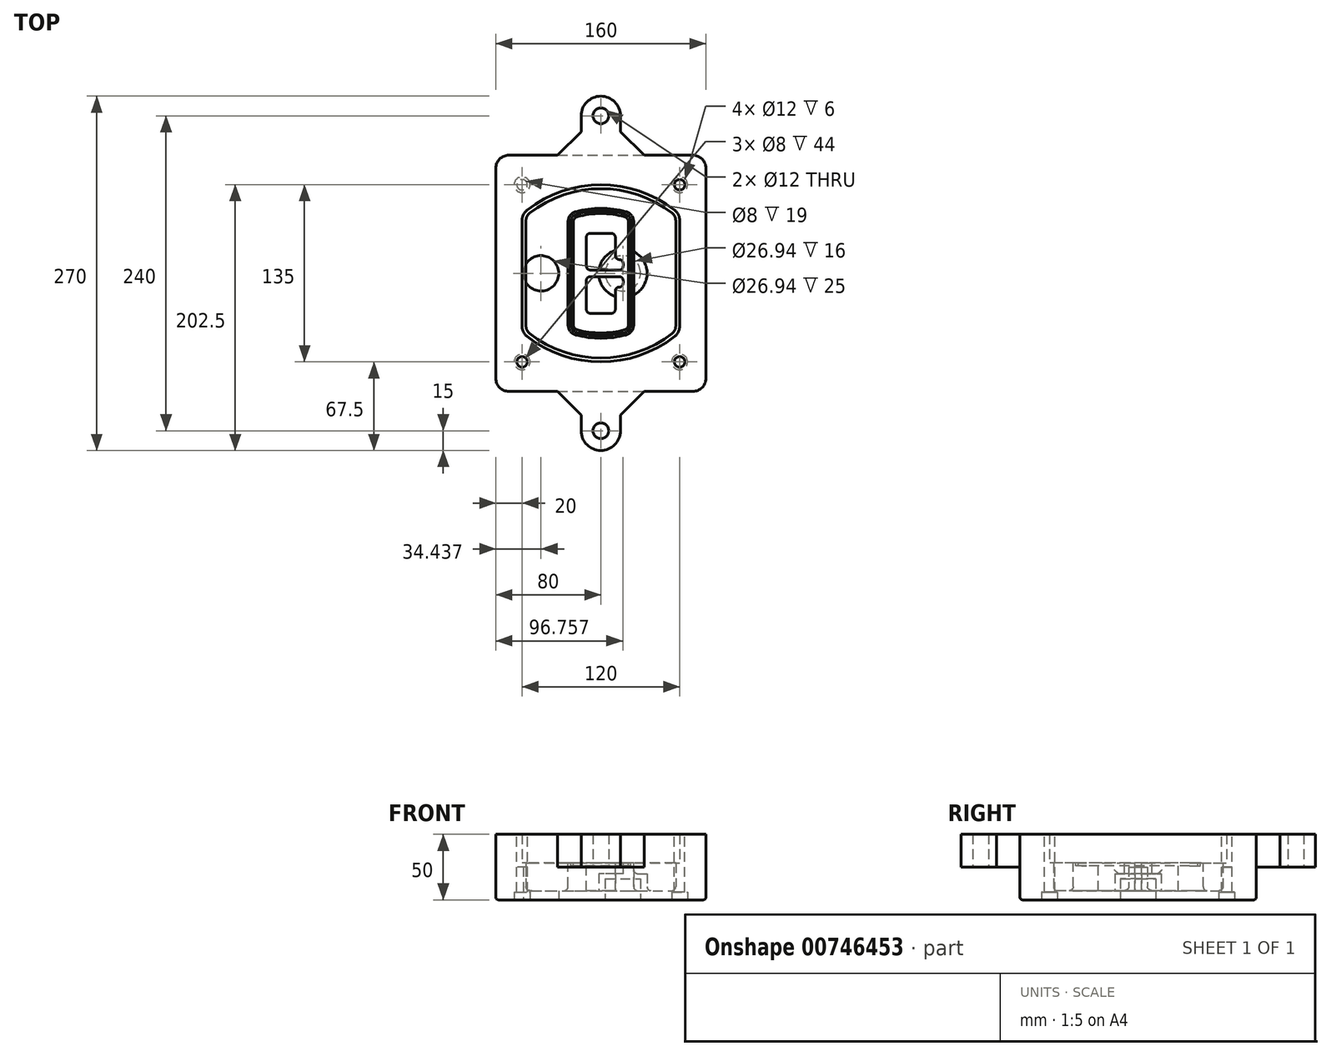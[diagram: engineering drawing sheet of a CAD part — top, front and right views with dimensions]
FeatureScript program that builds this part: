
annotation { "Feature Type Name" : "Feature", "Feature Type Description" : "" }
export const myFeature = defineFeature(function(context is Context, id is Id, definition is map)
    precondition{}
    {
        {
            var Q0;
            Q0=qCreatedBy(makeId("Top.planeOp"),FACE);
            var sketch = newSketch(context, id + "F0", { "sketchPlane" : qUnion([Q0])});
            skPoint(sketch, "E0.rect.middle", {"position": v(0, 0) * mm});
            skLineSegment(sketch, "E1.bottom", {"start": v(-70, -90) * mm, "end": v(70, -90) * mm});
            skLineSegment(sketch, "E1.top", {"start": v(-70, 90) * mm, "end": v(70, 90) * mm});
            skLineSegment(sketch, "E1.left", {"start": v(-80, -80) * mm, "end": v(-80, 80) * mm});
            skLineSegment(sketch, "E1.right", {"start": v(80, -80) * mm, "end": v(80, 80) * mm});
            skLineSegment(sketch, "E2", {"start": v(-80, 90) * mm, "end": v(80, -90) * mm, "construction": true});
            skLineSegment(sketch, "E3", {"start": v(80, 90) * mm, "end": v(-80, -90) * mm, "construction": true});
            skCircle(sketch, "E4", {"center": v(-60, 67.5) * mm, "radius": 4 * mm});
            skCircle(sketch, "E5", {"center": v(60, 67.5) * mm, "radius": 4 * mm});
            skCircle(sketch, "E6", {"center": v(60, -67.5) * mm, "radius": 4 * mm});
            skCircle(sketch, "E7", {"center": v(-60, -67.5) * mm, "radius": 4 * mm});
            skLineSegment(sketch, "E8", {"start": v(-60, 67.5) * mm, "end": v(60, 67.5) * mm, "construction": true});
            skLineSegment(sketch, "E9", {"start": v(60, 67.5) * mm, "end": v(60, -67.5) * mm, "construction": true});
            skLineSegment(sketch, "E10", {"start": v(60, -67.5) * mm, "end": v(-60, -67.5) * mm, "construction": true});
            skLineSegment(sketch, "E11", {"start": v(-60, -67.5) * mm, "end": v(-60, 67.5) * mm, "construction": true});
            skLineSegment(sketch, "E12", {"start": v(-60, 40.3) * mm, "end": v(-60, -40.3) * mm});
            skLineSegment(sketch, "E13", {"start": v(60, 40.3) * mm, "end": v(60, -40.3) * mm});
            skArc(sketch, "E14", {"start": v(56.15, 48.18) * mm, "mid": v(0, 67.5) * mm, "end": v(-56.15, 48.18) * mm});
            skArc(sketch, "E15", {"start": v(-56.15, -48.18) * mm, "mid": v(0, -67.5) * mm, "end": v(56.15, -48.18) * mm});
            skLineSegment(sketch, "E16", {"start": v(-60, 0) * mm, "end": v(60, 0) * mm, "construction": true});
            skPoint(sketch, "E17.visualSharp", {"position": v(-60, -45) * mm});
            skArc(sketch, "E17.filletArc", {"start": v(-60, -40.3) * mm, "mid": v(-58.99, -44.68) * mm, "end": v(-56.15, -48.18) * mm});
            skPoint(sketch, "E18.visualSharp", {"position": v(-60, 45) * mm});
            skArc(sketch, "E18.filletArc", {"start": v(-56.15, 48.18) * mm, "mid": v(-58.99, 44.68) * mm, "end": v(-60, 40.3) * mm});
            skPoint(sketch, "E19.visualSharp", {"position": v(60, 45) * mm});
            skArc(sketch, "E19.filletArc", {"start": v(60, 40.3) * mm, "mid": v(58.99, 44.68) * mm, "end": v(56.15, 48.18) * mm});
            skPoint(sketch, "E20.visualSharp", {"position": v(60, -45) * mm});
            skArc(sketch, "E20.filletArc", {"start": v(56.15, -48.18) * mm, "mid": v(58.99, -44.68) * mm, "end": v(60, -40.3) * mm});
            skPoint(sketch, "E21.visualSharp", {"position": v(-80, 90) * mm});
            skArc(sketch, "E21.filletArc", {"start": v(-70, 90) * mm, "mid": v(-77.07, 87.07) * mm, "end": v(-80, 80) * mm});
            skPoint(sketch, "E22.visualSharp", {"position": v(80, 90) * mm});
            skArc(sketch, "E22.filletArc", {"start": v(80, 80) * mm, "mid": v(77.07, 87.07) * mm, "end": v(70, 90) * mm});
            skPoint(sketch, "E23.visualSharp", {"position": v(80, -90) * mm});
            skArc(sketch, "E23.filletArc", {"start": v(70, -90) * mm, "mid": v(77.07, -87.07) * mm, "end": v(80, -80) * mm});
            skPoint(sketch, "E24.visualSharp", {"position": v(-80, -90) * mm});
            skArc(sketch, "E24.filletArc", {"start": v(-80, -80) * mm, "mid": v(-77.07, -87.07) * mm, "end": v(-70, -90) * mm});
            skArc(sketch, "E25.0", {"start": v(57, 40.3) * mm, "mid": v(56.3, 43.36) * mm, "end": v(54.3, 45.81) * mm});
            skLineSegment(sketch, "E25.1", {"start": v(57, 40.3) * mm, "end": v(57, -40.3) * mm});
            skArc(sketch, "E25.2", {"start": v(54.3, -45.81) * mm, "mid": v(56.3, -43.36) * mm, "end": v(57, -40.3) * mm});
            skArc(sketch, "E25.3", {"start": v(-54.3, -45.81) * mm, "mid": v(0, -64.5) * mm, "end": v(54.3, -45.81) * mm});
            skArc(sketch, "E25.4", {"start": v(-57, -40.3) * mm, "mid": v(-56.3, -43.36) * mm, "end": v(-54.3, -45.81) * mm});
            skArc(sketch, "E25.5", {"start": v(54.3, 45.81) * mm, "mid": v(0, 64.5) * mm, "end": v(-54.3, 45.81) * mm});
            skLineSegment(sketch, "E25.6", {"start": v(-57, 40.3) * mm, "end": v(-57, -40.3) * mm});
            skArc(sketch, "E25.7", {"start": v(-54.3, 45.81) * mm, "mid": v(-56.3, 43.36) * mm, "end": v(-57, 40.3) * mm});
            skArc(sketch, "E26.0", {"start": v(-58.62, 51.33) * mm, "mid": v(-62.58, 46.43) * mm, "end": v(-64, 40.3) * mm});
            skArc(sketch, "E26.1", {"start": v(58.62, 51.33) * mm, "mid": v(0, 71.5) * mm, "end": v(-58.62, 51.33) * mm});
            skArc(sketch, "E26.2", {"start": v(64, 40.3) * mm, "mid": v(62.58, 46.43) * mm, "end": v(58.62, 51.33) * mm});
            skLineSegment(sketch, "E26.3", {"start": v(64, 40.3) * mm, "end": v(64, -40.3) * mm});
            skArc(sketch, "E26.4", {"start": v(58.62, -51.33) * mm, "mid": v(62.58, -46.43) * mm, "end": v(64, -40.3) * mm});
            skLineSegment(sketch, "E26.5", {"start": v(-64, 40.3) * mm, "end": v(-64, -40.3) * mm});
            skArc(sketch, "E26.6", {"start": v(-58.62, -51.33) * mm, "mid": v(0, -71.5) * mm, "end": v(58.62, -51.33) * mm});
            skArc(sketch, "E26.7", {"start": v(-64, -40.3) * mm, "mid": v(-62.58, -46.43) * mm, "end": v(-58.62, -51.33) * mm});
            skSolve(sketch);
        }
        {
            var Q0;
            Q0=makeQuery(id+"F0.imprint","IMPRINT",FACE,{"disambiguationData":[TD([[makeQuery(id+"F0.imprint","IMPRINT",EDGE,{"derivedFrom":sQuery(id+"F0.wireOp",EDGE,"E1.bottom")}),1.0]])]});
            var Q1;
            Q1=makeQuery(id+"F0.imprint","IMPRINT",FACE,{"disambiguationData":[TD([[makeQuery(id+"F0.imprint","IMPRINT",EDGE,{"derivedFrom":sQuery(id+"F0.wireOp",EDGE,"E12")}),1.0]])]});
            var Q2;
            Q2=makeQuery(id+"F0.imprint","IMPRINT",FACE,{"disambiguationData":[TD([[makeQuery(id+"F0.imprint","IMPRINT",EDGE,{"derivedFrom":sQuery(id+"F0.wireOp",EDGE,"E25.0")}),1.0]])]});
            var Q3;
            Q3=makeQuery(id+"F0.imprint","IMPRINT",FACE,{"disambiguationData":[TD([[makeQuery(id+"F0.imprint","IMPRINT",EDGE,{"derivedFrom":sQuery(id+"F0.wireOp",EDGE,"E12")}),-1.0]])]});
            extrude(context, id + "F1", {"entities" : qUnion([Q0, Q1, Q2, Q3]), "oppositeDirection" : true, "depth" : 25 * mm});
        }
        {
            var Q0;
            Q0=makeQuery(id+"F0.imprint","IMPRINT",FACE,{"disambiguationData":[TD([[makeQuery(id+"F0.imprint","IMPRINT",EDGE,{"derivedFrom":sQuery(id+"F0.wireOp",EDGE,"E12")}),1.0]])]});
            extrude(context, id + "F2", {"entities" : qUnion([Q0]), "operationType" : NewBodyOperationType.ADD, "depth" : 3 * mm});
        }
        {
            var Q0;
            Q0=makeQuery(id+"F0.imprint","IMPRINT",FACE,{"disambiguationData":[TD([[makeQuery(id+"F0.imprint","IMPRINT",EDGE,{"derivedFrom":sQuery(id+"F0.wireOp",EDGE,"E25.0")}),1.0]])]});
            extrude(context, id + "F3", {"entities" : qUnion([Q0]), "operationType" : NewBodyOperationType.REMOVE, "oppositeDirection" : true, "depth" : 18 * mm});
        }
        {
            var Q0;
            Q0=makeQuery(id+"F2.opExtrude","CAP_FACE",FACE,{"disambiguationData":[OSD([sQuery(id+"F0.wireOp",EDGE,"E12"),sQuery(id+"F0.wireOp",EDGE,"E13"),sQuery(id+"F0.wireOp",EDGE,"E14"),sQuery(id+"F0.wireOp",EDGE,"E15"),sQuery(id+"F0.wireOp",EDGE,"E17.filletArc"),sQuery(id+"F0.wireOp",EDGE,"E18.filletArc"),sQuery(id+"F0.wireOp",EDGE,"E19.filletArc"),sQuery(id+"F0.wireOp",EDGE,"E20.filletArc"),sQuery(id+"F0.wireOp",EDGE,"E25.0"),sQuery(id+"F0.wireOp",EDGE,"E25.1"),sQuery(id+"F0.wireOp",EDGE,"E25.2"),sQuery(id+"F0.wireOp",EDGE,"E25.3"),sQuery(id+"F0.wireOp",EDGE,"E25.4"),sQuery(id+"F0.wireOp",EDGE,"E25.5"),sQuery(id+"F0.wireOp",EDGE,"E25.6"),sQuery(id+"F0.wireOp",EDGE,"E25.7")])],"isStart":false});
            var sketch = newSketch(context, id + "F4", { "sketchPlane" : qUnion([Q0])});
            skArc(sketch, "E27.0", {"start": v(-19.08, -46.97) * mm, "mid": v(0, -49.5) * mm, "end": v(19.08, -46.97) * mm});
            skArc(sketch, "E28.0", {"start": v(19.08, 46.97) * mm, "mid": v(0, 49.5) * mm, "end": v(-19.08, 46.97) * mm});
            skLineSegment(sketch, "E29", {"start": v(-25, 39.25) * mm, "end": v(-25, -39.25) * mm});
            skLineSegment(sketch, "E30", {"start": v(25, 39.25) * mm, "end": v(25, -39.25) * mm});
            skLineSegment(sketch, "E31", {"start": v(-25, 45.1) * mm, "end": v(25, 45.1) * mm, "construction": true});
            skLineSegment(sketch, "E32", {"start": v(-25, -45.1) * mm, "end": v(25, -45.1) * mm, "construction": true});
            skPoint(sketch, "E33.visualSharp", {"position": v(-25, 45.1) * mm});
            skArc(sketch, "E33.filletArc", {"start": v(-19.08, 46.97) * mm, "mid": v(-23.35, 44.11) * mm, "end": v(-25, 39.25) * mm});
            skPoint(sketch, "E34.visualSharp", {"position": v(25, 45.1) * mm});
            skArc(sketch, "E34.filletArc", {"start": v(25, 39.25) * mm, "mid": v(23.35, 44.11) * mm, "end": v(19.08, 46.97) * mm});
            skPoint(sketch, "E35.visualSharp", {"position": v(25, -45.1) * mm});
            skArc(sketch, "E35.filletArc", {"start": v(19.08, -46.97) * mm, "mid": v(23.35, -44.11) * mm, "end": v(25, -39.25) * mm});
            skPoint(sketch, "E36.visualSharp", {"position": v(-25, -45.1) * mm});
            skArc(sketch, "E36.filletArc", {"start": v(-25, -39.25) * mm, "mid": v(-23.35, -44.11) * mm, "end": v(-19.08, -46.97) * mm});
            skArc(sketch, "E37.0", {"start": v(54.3, 45.81) * mm, "mid": v(0, 64.5) * mm, "end": v(-54.3, 45.81) * mm});
            skArc(sketch, "E37.1", {"start": v(-54.3, 45.81) * mm, "mid": v(-56.3, 43.36) * mm, "end": v(-57, 40.3) * mm});
            skLineSegment(sketch, "E37.2", {"start": v(-57, 40.3) * mm, "end": v(-57, -40.3) * mm});
            skArc(sketch, "E37.3", {"start": v(-57, -40.3) * mm, "mid": v(-56.3, -43.36) * mm, "end": v(-54.3, -45.81) * mm});
            skArc(sketch, "E37.4", {"start": v(-54.3, -45.81) * mm, "mid": v(0, -64.5) * mm, "end": v(54.3, -45.81) * mm});
            skArc(sketch, "E37.5", {"start": v(54.3, -45.81) * mm, "mid": v(56.3, -43.36) * mm, "end": v(57, -40.3) * mm});
            skLineSegment(sketch, "E37.6", {"start": v(57, 40.3) * mm, "end": v(57, -40.3) * mm});
            skArc(sketch, "E37.7", {"start": v(57, 40.3) * mm, "mid": v(56.3, 43.36) * mm, "end": v(54.3, 45.81) * mm});
            skLineSegment(sketch, "E38.0", {"start": v(23, 39.25) * mm, "end": v(23, -39.25) * mm});
            skArc(sketch, "E38.1", {"start": v(18.56, -45.04) * mm, "mid": v(21.76, -42.9) * mm, "end": v(23, -39.25) * mm});
            skArc(sketch, "E38.2", {"start": v(-18.56, -45.04) * mm, "mid": v(0, -47.5) * mm, "end": v(18.56, -45.04) * mm});
            skArc(sketch, "E38.3", {"start": v(-23, -39.25) * mm, "mid": v(-21.76, -42.9) * mm, "end": v(-18.56, -45.04) * mm});
            skLineSegment(sketch, "E38.4", {"start": v(-23, 39.25) * mm, "end": v(-23, -39.25) * mm});
            skArc(sketch, "E38.5", {"start": v(23, 39.25) * mm, "mid": v(21.76, 42.9) * mm, "end": v(18.56, 45.04) * mm});
            skArc(sketch, "E38.6", {"start": v(-18.56, 45.04) * mm, "mid": v(-21.76, 42.9) * mm, "end": v(-23, 39.25) * mm});
            skArc(sketch, "E38.7", {"start": v(18.56, 45.04) * mm, "mid": v(0, 47.5) * mm, "end": v(-18.56, 45.04) * mm});
            skArc(sketch, "E39.0", {"start": v(21, 39.25) * mm, "mid": v(20.18, 41.68) * mm, "end": v(18.04, 43.1) * mm});
            skLineSegment(sketch, "E39.1", {"start": v(21, 39.25) * mm, "end": v(21, -39.25) * mm});
            skArc(sketch, "E39.2", {"start": v(18.04, -43.1) * mm, "mid": v(20.18, -41.68) * mm, "end": v(21, -39.25) * mm});
            skArc(sketch, "E39.3", {"start": v(-18.04, -43.1) * mm, "mid": v(0, -45.5) * mm, "end": v(18.04, -43.1) * mm});
            skArc(sketch, "E39.4", {"start": v(-21, -39.25) * mm, "mid": v(-20.18, -41.68) * mm, "end": v(-18.04, -43.1) * mm});
            skArc(sketch, "E39.5", {"start": v(18.04, 43.1) * mm, "mid": v(0, 45.5) * mm, "end": v(-18.04, 43.1) * mm});
            skLineSegment(sketch, "E39.6", {"start": v(-21, 39.25) * mm, "end": v(-21, -39.25) * mm});
            skArc(sketch, "E39.7", {"start": v(-18.04, 43.1) * mm, "mid": v(-20.18, 41.68) * mm, "end": v(-21, 39.25) * mm});
            skLineSegment(sketch, "E40", {"start": v(-25, 0) * mm, "end": v(25, 0) * mm, "construction": true});
            skLineSegment(sketch, "E41", {"start": v(-11, 5.5) * mm, "end": v(-11, 27.5) * mm});
            skLineSegment(sketch, "E42", {"start": v(-8, 30.5) * mm, "end": v(8, 30.5) * mm});
            skLineSegment(sketch, "E43", {"start": v(11, 27.5) * mm, "end": v(11, 13.5) * mm});
            skLineSegment(sketch, "E44", {"start": v(14, 10.5) * mm, "end": v(14, 10.5) * mm});
            skLineSegment(sketch, "E45", {"start": v(17, 7.5) * mm, "end": v(17, 5.5) * mm});
            skLineSegment(sketch, "E46", {"start": v(14, 2.5) * mm, "end": v(-8, 2.5) * mm});
            skPoint(sketch, "E47.visualSharp", {"position": v(-11, 30.5) * mm});
            skArc(sketch, "E47.filletArc", {"start": v(-8, 30.5) * mm, "mid": v(-10.12, 29.62) * mm, "end": v(-11, 27.5) * mm});
            skPoint(sketch, "E48.visualSharp", {"position": v(11, 30.5) * mm});
            skArc(sketch, "E48.filletArc", {"start": v(11, 27.5) * mm, "mid": v(10.12, 29.62) * mm, "end": v(8, 30.5) * mm});
            skPoint(sketch, "E49.visualSharp", {"position": v(11, 10.5) * mm});
            skArc(sketch, "E49.filletArc", {"start": v(11, 13.5) * mm, "mid": v(11.88, 11.38) * mm, "end": v(14, 10.5) * mm});
            skPoint(sketch, "E50.visualSharp", {"position": v(17, 10.5) * mm});
            skArc(sketch, "E50.filletArc", {"start": v(17, 7.5) * mm, "mid": v(16.12, 9.62) * mm, "end": v(14, 10.5) * mm});
            skPoint(sketch, "E51.visualSharp", {"position": v(17, 2.5) * mm});
            skArc(sketch, "E51.filletArc", {"start": v(14, 2.5) * mm, "mid": v(16.12, 3.38) * mm, "end": v(17, 5.5) * mm});
            skPoint(sketch, "E52.visualSharp", {"position": v(-11, 2.5) * mm});
            skArc(sketch, "E52.filletArc", {"start": v(-11, 5.5) * mm, "mid": v(-10.12, 3.38) * mm, "end": v(-8, 2.5) * mm});
            skLineSegment(sketch, "E53.0.MirrorCS", {"start": v(14, -2.5) * mm, "end": v(-8, -2.5) * mm});
            skArc(sketch, "E54.0.MirrorCS", {"start": v(-11, -5.5) * mm, "mid": v(-10.12, -3.38) * mm, "end": v(-8, -2.5) * mm});
            skLineSegment(sketch, "E55.0.MirrorCS", {"start": v(-11, -5.5) * mm, "end": v(-11, -27.5) * mm});
            skArc(sketch, "E56.0.MirrorCS", {"start": v(-8, -30.5) * mm, "mid": v(-10.12, -29.62) * mm, "end": v(-11, -27.5) * mm});
            skLineSegment(sketch, "E57.0.MirrorCS", {"start": v(-8, -30.5) * mm, "end": v(8, -30.5) * mm});
            skArc(sketch, "E58.0.MirrorCS", {"start": v(11, -27.5) * mm, "mid": v(10.12, -29.62) * mm, "end": v(8, -30.5) * mm});
            skLineSegment(sketch, "E59.0.MirrorCS", {"start": v(11, -27.5) * mm, "end": v(11, -13.5) * mm});
            skArc(sketch, "E60.0.MirrorCS", {"start": v(11, -13.5) * mm, "mid": v(11.88, -11.38) * mm, "end": v(14, -10.5) * mm});
            skArc(sketch, "E61.0.MirrorCS", {"start": v(17, -7.5) * mm, "mid": v(16.12, -9.62) * mm, "end": v(14, -10.5) * mm});
            skLineSegment(sketch, "E62.0.MirrorCS", {"start": v(17, -7.5) * mm, "end": v(17, -5.5) * mm});
            skArc(sketch, "E63.0.MirrorCS", {"start": v(14, -2.5) * mm, "mid": v(16.12, -3.38) * mm, "end": v(17, -5.5) * mm});
            skSolve(sketch);
        }
        {
            var Q0;
            Q0=makeQuery(id+"F4.imprint","IMPRINT",FACE,{"disambiguationData":[TD([[makeQuery(id+"F4.imprint","IMPRINT",EDGE,{"derivedFrom":sQuery(id+"F4.wireOp",EDGE,"E27.0")}),1.0]])]});
            var Q1;
            Q1=makeQuery(id+"F4.imprint","IMPRINT",FACE,{"disambiguationData":[TD([[makeQuery(id+"F4.imprint","IMPRINT",EDGE,{"derivedFrom":sQuery(id+"F4.wireOp",EDGE,"E38.0")}),-1.0]])]});
            var Q2;
            Q2=makeQuery(id+"F4.imprint","IMPRINT",FACE,{"disambiguationData":[TD([[makeQuery(id+"F4.imprint","IMPRINT",EDGE,{"derivedFrom":sQuery(id+"F4.wireOp",EDGE,"E39.0")}),1.0]])]});
            extrude(context, id + "F5", {"entities" : qUnion([Q0, Q1, Q2]), "operationType" : NewBodyOperationType.ADD, "endBound" : BoundingType.UP_TO_NEXT, "oppositeDirection" : true, "depth" : 25 * mm});
        }
        {
            var Q0;
            Q0=makeQuery(id+"F4.imprint","IMPRINT",FACE,{"disambiguationData":[TD([[makeQuery(id+"F4.imprint","IMPRINT",EDGE,{"derivedFrom":sQuery(id+"F4.wireOp",EDGE,"E38.0")}),-1.0]])]});
            extrude(context, id + "F6", {"entities" : qUnion([Q0]), "operationType" : NewBodyOperationType.REMOVE, "oppositeDirection" : true, "depth" : 2 * mm});
        }
        {
            var Q0;
            Q0=makeQuery(id+"F1.opExtrude","CAP_FACE",FACE,{"disambiguationData":[OSD([sQuery(id+"F0.wireOp",EDGE,"E1.bottom"),sQuery(id+"F0.wireOp",EDGE,"E1.top"),sQuery(id+"F0.wireOp",EDGE,"E1.left"),sQuery(id+"F0.wireOp",EDGE,"E1.right"),sQuery(id+"F0.wireOp",EDGE,"E4"),sQuery(id+"F0.wireOp",EDGE,"E5"),sQuery(id+"F0.wireOp",EDGE,"E6"),sQuery(id+"F0.wireOp",EDGE,"E7"),sQuery(id+"F0.wireOp",EDGE,"E21.filletArc"),sQuery(id+"F0.wireOp",EDGE,"E22.filletArc"),sQuery(id+"F0.wireOp",EDGE,"E23.filletArc"),sQuery(id+"F0.wireOp",EDGE,"E24.filletArc")])],"isStart":false});
            var sketch = newSketch(context, id + "F7", { "sketchPlane" : qUnion([Q0])});
            skCircle(sketch, "E64", {"center": v(16.76, 0) * mm, "radius": 13.47 * mm});
            skCircle(sketch, "E65", {"center": v(-45.56, 0) * mm, "radius": 13.47 * mm});
            skLineSegment(sketch, "E66", {"start": v(80, 0) * mm, "end": v(-80, 0) * mm});
            skCircle(sketch, "E67", {"center": v(16.76, 0) * mm, "radius": 18.47 * mm});
            skCircle(sketch, "E68", {"center": v(60, -67.5) * mm, "radius": 6 * mm});
            skCircle(sketch, "E69", {"center": v(-60, -67.5) * mm, "radius": 6 * mm});
            skCircle(sketch, "E70", {"center": v(-60, 67.5) * mm, "radius": 6 * mm});
            skCircle(sketch, "E71", {"center": v(60, 67.5) * mm, "radius": 6 * mm});
            skSolve(sketch);
        }
        {
            var Q0;
            {var subQ1=sQuery(id+"F7.wireOp",EDGE,"E66");var subQ4=sQuery(id+"F7.wireOp",EDGE,"E64");var subQ6=makeQuery(id+"F7.imprint","INTERSECT",VERTEX,{"disambiguationData":[OD(0.0)],"derivedFrom":[subQ4,subQ1]});Q0=makeQuery(id+"F7.imprint","IMPRINT",FACE,{"disambiguationData":[TD([[makeQuery(id+"F7.imprint","IMPRINT",EDGE,{"disambiguationData":[TD([[subQ6,-1.0]])],"derivedFrom":subQ4}),-1.0]])]});}
            var Q1;
            {var subQ0=sQuery(id+"F7.wireOp",EDGE,"E66");var subQ1=sQuery(id+"F7.wireOp",EDGE,"E64");var subQ3=makeQuery(id+"F7.imprint","INTERSECT",VERTEX,{"disambiguationData":[OD(0.0)],"derivedFrom":[subQ1,subQ0]});Q1=makeQuery(id+"F7.imprint","IMPRINT",FACE,{"disambiguationData":[TD([[makeQuery(id+"F7.imprint","IMPRINT",EDGE,{"disambiguationData":[TD([[subQ3,-1.0]])],"derivedFrom":subQ1}),1.0]])]});}
            var Q2;
            {var subQ0=sQuery(id+"F7.wireOp",EDGE,"E66");var subQ1=sQuery(id+"F7.wireOp",EDGE,"E64");var subQ3=makeQuery(id+"F7.imprint","INTERSECT",VERTEX,{"disambiguationData":[OD(0.0)],"derivedFrom":[subQ1,subQ0]});Q2=makeQuery(id+"F7.imprint","IMPRINT",FACE,{"disambiguationData":[TD([[makeQuery(id+"F7.imprint","IMPRINT",EDGE,{"disambiguationData":[TD([[subQ3,1.0]])],"derivedFrom":subQ1}),1.0]])]});}
            var Q3;
            {var subQ1=sQuery(id+"F7.wireOp",EDGE,"E66");var subQ4=sQuery(id+"F7.wireOp",EDGE,"E64");var subQ6=makeQuery(id+"F7.imprint","INTERSECT",VERTEX,{"disambiguationData":[OD(0.0)],"derivedFrom":[subQ4,subQ1]});Q3=makeQuery(id+"F7.imprint","IMPRINT",FACE,{"disambiguationData":[TD([[makeQuery(id+"F7.imprint","IMPRINT",EDGE,{"disambiguationData":[TD([[subQ6,1.0]])],"derivedFrom":subQ4}),-1.0]])]});}
            extrude(context, id + "F8", {"entities" : qUnion([Q0, Q1, Q2, Q3]), "operationType" : NewBodyOperationType.ADD, "oppositeDirection" : true, "depth" : 20 * mm});
        }
        {
            var Q0;
            {var subQ0=sQuery(id+"F7.wireOp",EDGE,"E66");var subQ1=sQuery(id+"F7.wireOp",EDGE,"E64");var subQ3=makeQuery(id+"F7.imprint","INTERSECT",VERTEX,{"disambiguationData":[OD(0.0)],"derivedFrom":[subQ1,subQ0]});Q0=makeQuery(id+"F7.imprint","IMPRINT",FACE,{"disambiguationData":[TD([[makeQuery(id+"F7.imprint","IMPRINT",EDGE,{"disambiguationData":[TD([[subQ3,-1.0]])],"derivedFrom":subQ1}),1.0]])]});}
            var Q1;
            {var subQ0=sQuery(id+"F7.wireOp",EDGE,"E66");var subQ1=sQuery(id+"F7.wireOp",EDGE,"E64");var subQ3=makeQuery(id+"F7.imprint","INTERSECT",VERTEX,{"disambiguationData":[OD(0.0)],"derivedFrom":[subQ1,subQ0]});Q1=makeQuery(id+"F7.imprint","IMPRINT",FACE,{"disambiguationData":[TD([[makeQuery(id+"F7.imprint","IMPRINT",EDGE,{"disambiguationData":[TD([[subQ3,1.0]])],"derivedFrom":subQ1}),1.0]])]});}
            extrude(context, id + "F9", {"entities" : qUnion([Q0, Q1]), "operationType" : NewBodyOperationType.REMOVE, "oppositeDirection" : true, "depth" : 16 * mm, "offsetDistance" : 25 * mm});
        }
        {
            var Q0;
            {var subQ0=sQuery(id+"F7.wireOp",EDGE,"E66");var subQ1=sQuery(id+"F7.wireOp",EDGE,"E65");var subQ3=makeQuery(id+"F7.imprint","INTERSECT",VERTEX,{"disambiguationData":[OD(0.0)],"derivedFrom":[subQ1,subQ0]});Q0=makeQuery(id+"F7.imprint","IMPRINT",FACE,{"disambiguationData":[TD([[makeQuery(id+"F7.imprint","IMPRINT",EDGE,{"disambiguationData":[TD([[subQ3,-1.0]])],"derivedFrom":subQ1}),1.0]])]});}
            var Q1;
            {var subQ0=sQuery(id+"F7.wireOp",EDGE,"E66");var subQ1=sQuery(id+"F7.wireOp",EDGE,"E65");var subQ3=makeQuery(id+"F7.imprint","INTERSECT",VERTEX,{"disambiguationData":[OD(0.0)],"derivedFrom":[subQ1,subQ0]});Q1=makeQuery(id+"F7.imprint","IMPRINT",FACE,{"disambiguationData":[TD([[makeQuery(id+"F7.imprint","IMPRINT",EDGE,{"disambiguationData":[TD([[subQ3,1.0]])],"derivedFrom":subQ1}),1.0]])]});}
            extrude(context, id + "F10", {"entities" : qUnion([Q0, Q1]), "operationType" : NewBodyOperationType.REMOVE, "oppositeDirection" : true, "depth" : 25 * mm});
        }
        {
            var Q0;
            Q0=makeQuery(id+"F7.imprint","IMPRINT",FACE,{"disambiguationData":[TD([[makeQuery(id+"F7.imprint","IMPRINT",EDGE,{"derivedFrom":sQuery(id+"F7.wireOp",EDGE,"E68")}),1.0]])]});
            var Q1;
            Q1=makeQuery(id+"F7.imprint","IMPRINT",FACE,{"disambiguationData":[TD([[makeQuery(id+"F7.imprint","IMPRINT",EDGE,{"derivedFrom":makeQuery(id+"F1.opExtrude","CAP_EDGE",EDGE,{"disambiguationData":[OSD([sQuery(id+"F0.wireOp",EDGE,"E5")])],"isStart":false})}),-1.0]])]});
            var Q2;
            Q2=makeQuery(id+"F7.imprint","IMPRINT",FACE,{"disambiguationData":[TD([[makeQuery(id+"F7.imprint","IMPRINT",EDGE,{"derivedFrom":sQuery(id+"F7.wireOp",EDGE,"E69")}),1.0]])]});
            var Q3;
            Q3=makeQuery(id+"F7.imprint","IMPRINT",FACE,{"disambiguationData":[TD([[makeQuery(id+"F7.imprint","IMPRINT",EDGE,{"derivedFrom":makeQuery(id+"F1.opExtrude","CAP_EDGE",EDGE,{"disambiguationData":[OSD([sQuery(id+"F0.wireOp",EDGE,"E4")])],"isStart":false})}),-1.0]])]});
            var Q4;
            Q4=makeQuery(id+"F7.imprint","IMPRINT",FACE,{"disambiguationData":[TD([[makeQuery(id+"F7.imprint","IMPRINT",EDGE,{"derivedFrom":sQuery(id+"F7.wireOp",EDGE,"E70")}),1.0]])]});
            var Q5;
            Q5=makeQuery(id+"F7.imprint","IMPRINT",FACE,{"disambiguationData":[TD([[makeQuery(id+"F7.imprint","IMPRINT",EDGE,{"derivedFrom":makeQuery(id+"F1.opExtrude","CAP_EDGE",EDGE,{"disambiguationData":[OSD([sQuery(id+"F0.wireOp",EDGE,"E7")])],"isStart":false})}),-1.0]])]});
            var Q6;
            Q6=makeQuery(id+"F7.imprint","IMPRINT",FACE,{"disambiguationData":[TD([[makeQuery(id+"F7.imprint","IMPRINT",EDGE,{"derivedFrom":sQuery(id+"F7.wireOp",EDGE,"E71")}),1.0]])]});
            var Q7;
            Q7=makeQuery(id+"F7.imprint","IMPRINT",FACE,{"disambiguationData":[TD([[makeQuery(id+"F7.imprint","IMPRINT",EDGE,{"derivedFrom":makeQuery(id+"F1.opExtrude","CAP_EDGE",EDGE,{"disambiguationData":[OSD([sQuery(id+"F0.wireOp",EDGE,"E6")])],"isStart":false})}),-1.0]])]});
            extrude(context, id + "F11", {"entities" : qUnion([Q0, Q1, Q2, Q3, Q4, Q5, Q6, Q7]), "operationType" : NewBodyOperationType.REMOVE, "oppositeDirection" : true, "depth" : 6 * mm});
        }
        {
            var Q0;
            Q0=makeQuery(id+"F3.boolean.opBoolean","COPY",EDGE,{"derivedFrom":makeQuery(id+"F3.opExtrude","CAP_EDGE",EDGE,{"disambiguationData":[OSD([sQuery(id+"F0.wireOp",EDGE,"E25.6")])],"isStart":false})});
            var Q1;
            Q1=makeQuery(id+"F8.boolean.opBoolean","INTERSECT",EDGE,{"derivedFrom":[makeQuery(id+"F5.opExtrude","SWEPT_FACE",FACE,{"disambiguationData":[OSD([sQuery(id+"F4.wireOp",EDGE,"E30")])]}),makeQuery(id+"F8.opExtrude","CAP_FACE",FACE,{"disambiguationData":[OSD([sQuery(id+"F7.wireOp",EDGE,"E67")])],"isStart":false})]});
            var Q2;
            Q2=makeQuery(id+"F8.boolean.opBoolean","INTERSECT",EDGE,{"disambiguationData":[OD(1.0)],"derivedFrom":[makeQuery(id+"F5.opExtrude","SWEPT_FACE",FACE,{"disambiguationData":[OSD([sQuery(id+"F4.wireOp",EDGE,"E30")])]}),makeQuery(id+"F8.opExtrude","SWEPT_FACE",FACE,{"disambiguationData":[OSD([sQuery(id+"F7.wireOp",EDGE,"E67")])]})]});
            var Q3;
            {var subQ0=sQuery(id+"F4.wireOp",EDGE,"E30");Q3=makeQuery(id+"F8.boolean.opBoolean","SPLIT",EDGE,{"disambiguationData":[TD([makeQuery(id+"F5.opExtrude","SWEPT_FACE",FACE,{"disambiguationData":[OSD([sQuery(id+"F4.wireOp",EDGE,"E35.filletArc")])]})])],"derivedFrom":makeQuery(id+"F5.opExtrude","CAP_EDGE",EDGE,{"disambiguationData":[OSD([subQ0])],"isStart":false})});}
            var Q4;
            {var subQ0=sQuery(id+"F0.wireOp",EDGE,"E25.7");var subQ1=sQuery(id+"F0.wireOp",EDGE,"E25.1");var subQ2=sQuery(id+"F0.wireOp",EDGE,"E25.6");var subQ3=sQuery(id+"F0.wireOp",EDGE,"E25.5");var subQ4=sQuery(id+"F0.wireOp",EDGE,"E25.4");var subQ5=sQuery(id+"F0.wireOp",EDGE,"E25.0");var subQ6=sQuery(id+"F0.wireOp",EDGE,"E25.2");var subQ7=sQuery(id+"F0.wireOp",EDGE,"E25.3");Q4=makeQuery(id+"F8.boolean.opBoolean","INTERSECT",EDGE,{"derivedFrom":[makeQuery(id+"F5.boolean.opBoolean","SPLIT",FACE,{"disambiguationData":[TD([makeQuery(id+"F2.opExtrude","SWEPT_FACE",FACE,{"disambiguationData":[OSD([subQ5])]})])],"derivedFrom":makeQuery(id+"F3.boolean.opBoolean","COPY",FACE,{"derivedFrom":makeQuery(id+"F3.opExtrude","CAP_FACE",FACE,{"disambiguationData":[OSD([subQ5,subQ1,subQ6,subQ7,subQ4,subQ3,subQ2,subQ0])],"isStart":false})})}),makeQuery(id+"F8.opExtrude","SWEPT_FACE",FACE,{"disambiguationData":[OSD([sQuery(id+"F7.wireOp",EDGE,"E67")])]})]});}
            var Q5;
            Q5=makeQuery(id+"F8.boolean.opBoolean","INTERSECT",EDGE,{"disambiguationData":[OD(0.0)],"derivedFrom":[makeQuery(id+"F5.opExtrude","SWEPT_FACE",FACE,{"disambiguationData":[OSD([sQuery(id+"F4.wireOp",EDGE,"E30")])]}),makeQuery(id+"F8.opExtrude","SWEPT_FACE",FACE,{"disambiguationData":[OSD([sQuery(id+"F7.wireOp",EDGE,"E67")])]})]});
            fillet(context, id + "F12", {"entities" : qUnion([Q0, Q1, Q2, Q3, Q4, Q5]), "radius" : 3 * mm, "tangentPropagation" : true, "allowEdgeOverflow" : false});
        }
        {
            var Q0;
            Q0=makeQuery(id+"F1.opExtrude","CAP_EDGE",EDGE,{"disambiguationData":[OSD([sQuery(id+"F0.wireOp",EDGE,"E1.bottom")])],"isStart":false});
            fillet(context, id + "F13", {"entities" : qUnion([Q0]), "radius" : 2 * mm, "tangentPropagation" : true, "allowEdgeOverflow" : false});
        }
        {
            var Q0;
            {var subQ0=sQuery(id+"F0.wireOp",EDGE,"E21.filletArc");var subQ1=sQuery(id+"F0.wireOp",EDGE,"E7");var subQ2=sQuery(id+"F0.wireOp",EDGE,"E6");var subQ3=sQuery(id+"F0.wireOp",EDGE,"E5");var subQ4=sQuery(id+"F0.wireOp",EDGE,"E4");var subQ5=sQuery(id+"F0.wireOp",EDGE,"E22.filletArc");var subQ6=sQuery(id+"F0.wireOp",EDGE,"E1.bottom");var subQ7=sQuery(id+"F0.wireOp",EDGE,"E1.right");var subQ8=sQuery(id+"F0.wireOp",EDGE,"E1.top");var subQ9=sQuery(id+"F0.wireOp",EDGE,"E1.left");var subQ10=sQuery(id+"F0.wireOp",EDGE,"E23.filletArc");var subQ11=sQuery(id+"F0.wireOp",EDGE,"E24.filletArc");Q0=makeQuery(id+"F2.boolean.opBoolean","SPLIT",FACE,{"disambiguationData":[TD([makeQuery(id+"F1.opExtrude","SWEPT_FACE",FACE,{"disambiguationData":[OSD([subQ6])]})])],"derivedFrom":makeQuery(id+"F1.opExtrude","CAP_FACE",FACE,{"disambiguationData":[OSD([subQ6,subQ8,subQ9,subQ7,subQ4,subQ3,subQ2,subQ1,subQ0,subQ5,subQ10,subQ11])],"isStart":true})});}
            var sketch = newSketch(context, id + "F14", { "sketchPlane" : qUnion([Q0])});
            skLineSegment(sketch, "E72.0", {"start": v(-70, 90) * mm, "end": v(70, 90) * mm});
            skArc(sketch, "E72.1", {"start": v(-70, 90) * mm, "mid": v(-77.07, 87.07) * mm, "end": v(-80, 80) * mm});
            skLineSegment(sketch, "E72.2", {"start": v(-80, -80) * mm, "end": v(-80, 80) * mm});
            skArc(sketch, "E72.3", {"start": v(-80, -80) * mm, "mid": v(-77.07, -87.07) * mm, "end": v(-70, -90) * mm});
            skLineSegment(sketch, "E72.4", {"start": v(-70, -90) * mm, "end": v(70, -90) * mm});
            skArc(sketch, "E72.5", {"start": v(70, -90) * mm, "mid": v(77.07, -87.07) * mm, "end": v(80, -80) * mm});
            skLineSegment(sketch, "E72.6", {"start": v(80, -80) * mm, "end": v(80, 80) * mm});
            skArc(sketch, "E72.7", {"start": v(80, 80) * mm, "mid": v(77.07, 87.07) * mm, "end": v(70, 90) * mm});
            skArc(sketch, "E72.8", {"start": v(56.15, 48.18) * mm, "mid": v(0, 67.5) * mm, "end": v(-56.15, 48.18) * mm});
            skCircle(sketch, "E72.10", {"center": v(-60, -67.5) * mm, "radius": 4 * mm});
            skCircle(sketch, "E72.11", {"center": v(60, -67.5) * mm, "radius": 4 * mm});
            skCircle(sketch, "E72.12", {"center": v(60, 67.5) * mm, "radius": 4 * mm});
            skArc(sketch, "E72.13", {"start": v(60, 40.3) * mm, "mid": v(58.99, 44.68) * mm, "end": v(56.15, 48.18) * mm});
            skLineSegment(sketch, "E72.14", {"start": v(60, 40.3) * mm, "end": v(60, -40.3) * mm});
            skArc(sketch, "E72.15", {"start": v(56.15, -48.18) * mm, "mid": v(58.99, -44.68) * mm, "end": v(60, -40.3) * mm});
            skArc(sketch, "E72.16", {"start": v(-60, -40.3) * mm, "mid": v(-58.99, -44.68) * mm, "end": v(-56.15, -48.18) * mm});
            skArc(sketch, "E72.17", {"start": v(-56.15, -48.18) * mm, "mid": v(0, -67.5) * mm, "end": v(56.15, -48.18) * mm});
            skLineSegment(sketch, "E72.18", {"start": v(-60, 40.3) * mm, "end": v(-60, -40.3) * mm});
            skArc(sketch, "E72.19", {"start": v(-56.15, 48.18) * mm, "mid": v(-58.99, 44.68) * mm, "end": v(-60, 40.3) * mm});
            skLineSegment(sketch, "E73", {"start": v(-33, 90) * mm, "end": v(-15, 108) * mm});
            skLineSegment(sketch, "E74", {"start": v(-15, 108) * mm, "end": v(-15, 120) * mm});
            skArc(sketch, "E75", {"start": v(15, 120) * mm, "mid": v(0, 135) * mm, "end": v(-15, 120) * mm});
            skLineSegment(sketch, "E76", {"start": v(15, 120) * mm, "end": v(15, 108) * mm});
            skLineSegment(sketch, "E77", {"start": v(15, 108) * mm, "end": v(33, 90) * mm});
            skCircle(sketch, "E78", {"center": v(0, 120) * mm, "radius": 6 * mm});
            skLineSegment(sketch, "E79", {"start": v(0, 120) * mm, "end": v(0, 90) * mm, "construction": true});
            skLineSegment(sketch, "E80", {"start": v(-80, 0) * mm, "end": v(80, 0) * mm, "construction": true});
            skLineSegment(sketch, "E81.MirrorCS", {"start": v(-15, -108) * mm, "end": v(-15, -120) * mm});
            skLineSegment(sketch, "E82.MirrorCS", {"start": v(15, -120) * mm, "end": v(15, -108) * mm});
            skLineSegment(sketch, "E83.MirrorCS", {"start": v(-33, -90) * mm, "end": v(-15, -108) * mm});
            skCircle(sketch, "E84.MirrorC", {"center": v(0, -120) * mm, "radius": 6 * mm});
            skLineSegment(sketch, "E85.MirrorCS", {"start": v(0, -120) * mm, "end": v(0, -90) * mm, "construction": true});
            skLineSegment(sketch, "E86.MirrorCS", {"start": v(15, -108) * mm, "end": v(33, -90) * mm});
            skArc(sketch, "E87.MirrorCS", {"start": v(15, -120) * mm, "mid": v(0, -135) * mm, "end": v(-15, -120) * mm});
            skLineSegment(sketch, "E88.MirrorCS", {"start": v(-64.25, 74.25) * mm, "end": v(64.25, 74.25) * mm});
            skSolve(sketch);
        }
        {
            var Q0;
            Q0 = qSketchRegion(id + "F14", true);
            extrude(context, id + "F15", {"entities" : qUnion([Q0]), "operationType" : NewBodyOperationType.ADD, "depth" : 25 * mm, "offsetDistance" : 25 * mm});
        }
    });
